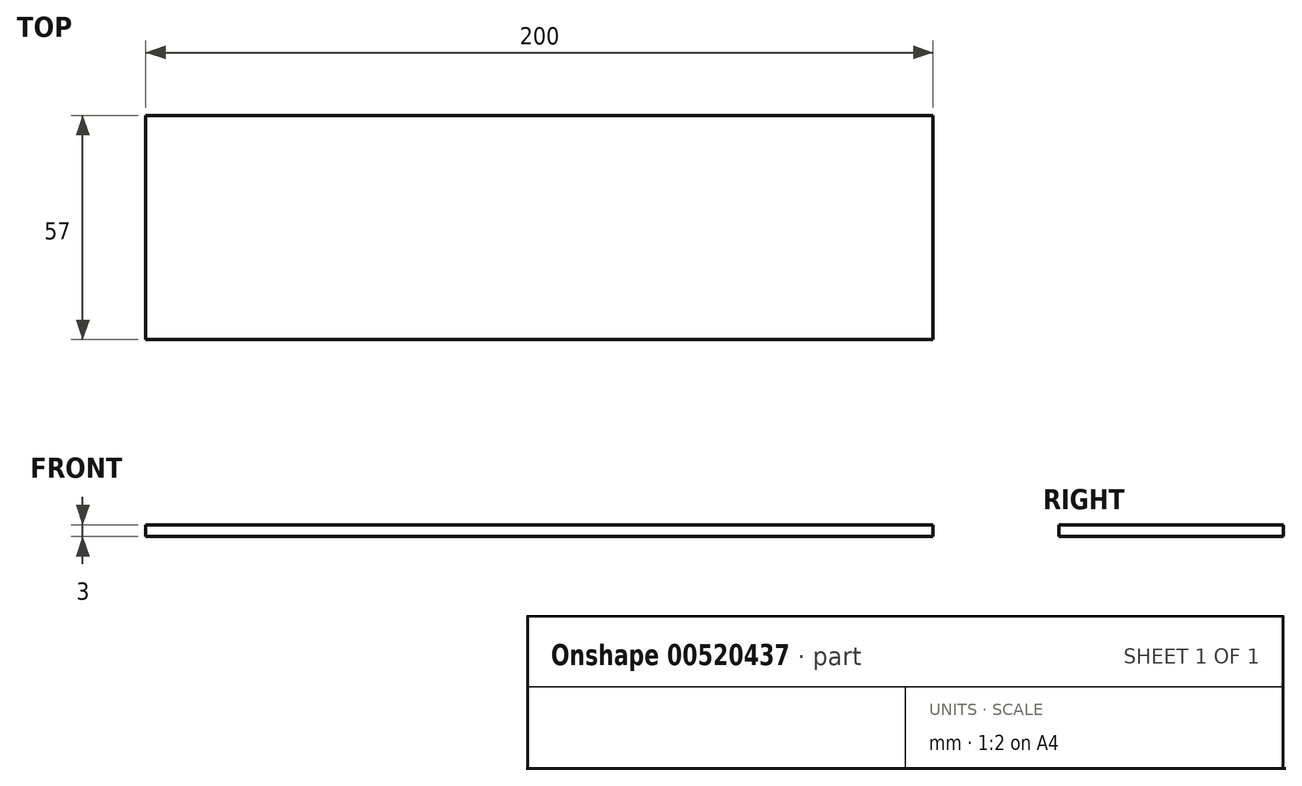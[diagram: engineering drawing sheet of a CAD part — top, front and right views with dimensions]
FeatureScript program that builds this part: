
annotation { "Feature Type Name" : "Feature", "Feature Type Description" : "" }
export const myFeature = defineFeature(function(context is Context, id is Id, definition is map)
    precondition{}
    {
        {
            var Q0;
            Q0=qCreatedBy(makeId("Top.planeOp"),FACE);
            var sketch = newSketch(context, id + "F0", { "sketchPlane" : qUnion([Q0])});
            skLineSegment(sketch, "E0.bottom", {"start": v(0, 0) * mm, "end": v(200, 0) * mm});
            skLineSegment(sketch, "E0.top", {"start": v(0, 57) * mm, "end": v(200, 57) * mm});
            skLineSegment(sketch, "E0.left", {"start": v(0, 0) * mm, "end": v(0, 57) * mm});
            skLineSegment(sketch, "E0.right", {"start": v(200, 0) * mm, "end": v(200, 57) * mm});
            skSolve(sketch);
        }
        {
            var Q0;
            Q0=makeQuery(id+"F0.imprint","IMPRINT",FACE,{"disambiguationData":[TD([[makeQuery(id+"F0.imprint","IMPRINT",EDGE,{"derivedFrom":sQuery(id+"F0.wireOp",EDGE,"E0.bottom")}),1.0]])]});
            extrude(context, id + "F1", {"entities" : qUnion([Q0]), "depth" : 3 * mm, "offsetDistance" : 25 * mm});
        }
    });
